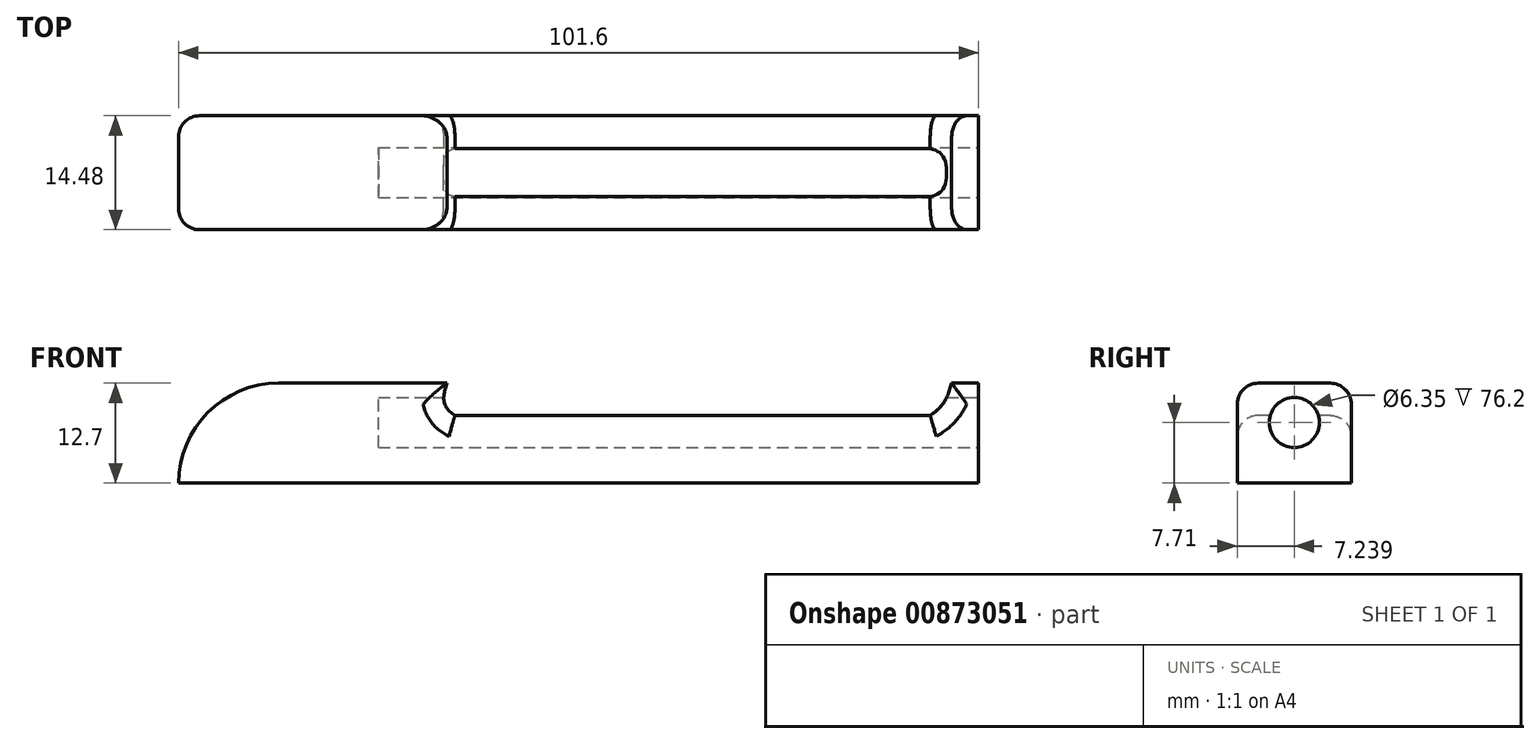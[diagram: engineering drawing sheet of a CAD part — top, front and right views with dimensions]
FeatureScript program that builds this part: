
annotation { "Feature Type Name" : "Feature", "Feature Type Description" : "" }
export const myFeature = defineFeature(function(context is Context, id is Id, definition is map)
    precondition{}
    {
        {
            var Q0;
            Q0=qCreatedBy(makeId("Front.planeOp"),FACE);
            var sketch = newSketch(context, id + "F0", { "sketchPlane" : qUnion([Q0])});
            skLineSegment(sketch, "E0.bottom", {"start": v(50.03, 39.41) * mm, "end": v(46.63, 39.41) * mm});
            skLineSegment(sketch, "E0.left", {"start": v(50.03, 39.41) * mm, "end": v(50.03, 26.71) * mm});
            skPoint(sketch, "E1.visualSharp", {"position": v(-51.57, 39.41) * mm});
            skArc(sketch, "E1.filletArc", {"start": v(-38.87, 39.41) * mm, "mid": v(-47.86, 35.7) * mm, "end": v(-51.57, 26.71) * mm});
            skLineSegment(sketch, "E2", {"start": v(-51.57, 26.71) * mm, "end": v(50.03, 26.71) * mm});
            skFitSpline(sketch, "E3", {"points": [v(-17.5, 39.41) * mm, v(-16.47, 35.32) * mm, v(41.38, 34.17) * mm, v(46.63, 39.41) * mm], "startDerivative": vector(-8, -26.35) * mm, "endDerivative": vector(7.67, 26.44) * mm});
            skLineSegment(sketch, "E4", {"start": v(-16.47, 35.32) * mm, "end": v(43.9, 35.32) * mm});
            skLineSegment(sketch, "E5.trimOffspring", {"start": v(-17.5, 39.41) * mm, "end": v(-38.87, 39.41) * mm});
            skSolve(sketch);
        }
        {
            var Q0;
            Q0 = qSketchRegion(id + "F0", true);
            extrude(context, id + "F1", {"entities" : qUnion([Q0]), "oppositeDirection" : true, "depth" : 14.48 * mm, "offsetDistance" : 25.4 * mm});
        }
        {
            var Q0;
            Q0=makeQuery(id+"F1.opExtrude","CAP_EDGE",EDGE,{"disambiguationData":[OSD([sQuery(id+"F0.wireOp",EDGE,"E4")])],"isStart":true});
            var Q1;
            Q1=makeQuery(id+"F1.opExtrude","CAP_EDGE",EDGE,{"disambiguationData":[OSD([sQuery(id+"F0.wireOp",EDGE,"E0.bottom")])],"isStart":true});
            var Q2;
            Q2=makeQuery(id+"F1.opExtrude","CAP_EDGE",EDGE,{"disambiguationData":[OSD([sQuery(id+"F0.wireOp",EDGE,"E5.trimOffspring")])],"isStart":true});
            var Q3;
            Q3=makeQuery(id+"F1.opExtrude","CAP_EDGE",EDGE,{"disambiguationData":[OSD([sQuery(id+"F0.wireOp",EDGE,"E4")])],"isStart":false});
            var Q4;
            Q4=makeQuery(id+"F1.opExtrude","CAP_EDGE",EDGE,{"disambiguationData":[OSD([sQuery(id+"F0.wireOp",EDGE,"E0.bottom")])],"isStart":false});
            var Q5;
            Q5=makeQuery(id+"F1.opExtrude","CAP_EDGE",EDGE,{"disambiguationData":[OSD([sQuery(id+"F0.wireOp",EDGE,"E5.trimOffspring")])],"isStart":false});
            var Q6;
            Q6=makeQuery(id+"F1.opExtrude","CAP_EDGE",EDGE,{"disambiguationData":[OSD([sQuery(id+"F0.wireOp",EDGE,"E3")])],"isStart":false});
            var Q7;
            Q7=makeQuery(id+"F1.opExtrude","CAP_EDGE",EDGE,{"disambiguationData":[OSD([sQuery(id+"F0.wireOp",EDGE,"E3")])],"isStart":true});
            fillet(context, id + "F2", {"entities" : qUnion([Q0, Q1, Q2, Q3, Q4, Q5, Q6, Q7]), "radius" : 2.67 * mm, "tangentPropagation" : true, "allowEdgeOverflow" : false});
        }
        {
            var Q0;
            Q0=makeQuery(id+"F1.opExtrude","SWEPT_FACE",FACE,{"disambiguationData":[OSD([sQuery(id+"F0.wireOp",EDGE,"E0.left")])]});
            var sketch = newSketch(context, id + "F3", { "sketchPlane" : qUnion([Q0])});
            skCircle(sketch, "E6", {"center": v(7.24, 34.42) * mm, "radius": 3.18 * mm});
            skPoint(sketch, "E7.trimOffspring.end.orphan", {"position": v(7.24, 39.41) * mm});
            skPoint(sketch, "E8.start.orphan", {"position": v(7.24, 26.71) * mm});
            skSolve(sketch);
        }
        {
            var Q0;
            Q0 = qSketchRegion(id + "F3", true);
            extrude(context, id + "F4", {"entities" : qUnion([Q0]), "operationType" : NewBodyOperationType.REMOVE, "oppositeDirection" : true, "depth" : 76.2 * mm, "offsetDistance" : 25.4 * mm});
        }
    });
